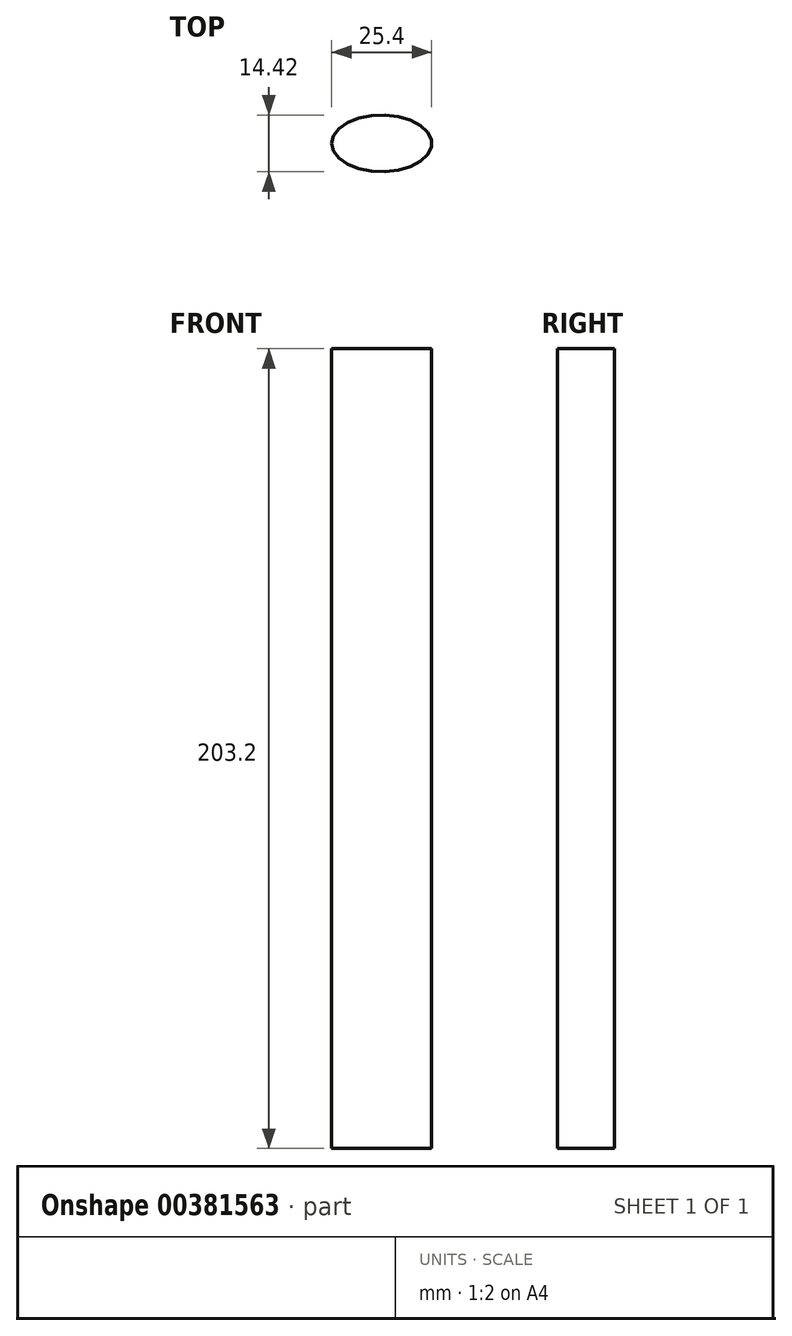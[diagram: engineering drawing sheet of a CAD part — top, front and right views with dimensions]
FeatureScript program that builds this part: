
annotation { "Feature Type Name" : "Feature", "Feature Type Description" : "" }
export const myFeature = defineFeature(function(context is Context, id is Id, definition is map)
    precondition{}
    {
        {
            var Q0;
            Q0=qCreatedBy(makeId("Top.planeOp"),FACE);
            var sketch = newSketch(context, id + "F0", { "sketchPlane" : qUnion([Q0])});
            skEllipse(sketch, "E0", {"center": v(0, 0) * mm, "majorRadius": 12.7 * mm, "minorRadius": 7.2 * mm, "majorAxis": v(-1, 0)});
            skFitSpline(sketch, "E1.0", {"points": [v(-11.32, 0.98) * mm, v(-11.49, 0) * mm, v(-11.32, -0.98) * mm, v(-10.87, -1.84) * mm, v(-10.3, -2.53) * mm, v(-9.57, -3.21) * mm, v(-8.41, -4.02) * mm, v(-6.95, -4.7) * mm, v(-5.63, -5.15) * mm, v(-4.22, -5.53) * mm, v(-2.73, -5.79) * mm, v(-1.18, -5.92) * mm, v(0, -5.95) * mm, v(1.18, -5.92) * mm, v(2.73, -5.79) * mm, v(4.22, -5.53) * mm, v(5.63, -5.15) * mm, v(6.95, -4.7) * mm, v(8.41, -4.02) * mm, v(9.57, -3.21) * mm, v(10.3, -2.53) * mm, v(10.87, -1.84) * mm, v(11.32, -0.98) * mm, v(11.49, 0) * mm, v(11.32, 0.98) * mm, v(10.87, 1.84) * mm, v(10.3, 2.53) * mm, v(9.57, 3.21) * mm, v(8.41, 4.02) * mm, v(6.95, 4.7) * mm, v(5.63, 5.15) * mm, v(4.22, 5.53) * mm, v(2.73, 5.79) * mm, v(1.18, 5.92) * mm, v(0, 5.95) * mm, v(-1.18, 5.92) * mm, v(-2.73, 5.79) * mm, v(-4.22, 5.53) * mm, v(-5.63, 5.15) * mm, v(-6.95, 4.7) * mm, v(-8.41, 4.02) * mm, v(-9.57, 3.21) * mm, v(-10.3, 2.53) * mm, v(-10.87, 1.84) * mm, v(-11.32, 0.98) * mm, v(-11.49, 0) * mm, v(-11.32, -0.98) * mm, v(-11.32, 0.98) * mm]});
            skSolve(sketch);
        }
        {
            var Q0;
            Q0=makeQuery(id+"F0.imprint","IMPRINT",FACE,{"disambiguationData":[TD([[makeQuery(id+"F0.imprint","IMPRINT",EDGE,{"derivedFrom":sQuery(id+"F0.wireOp",EDGE,"E0")}),1.0]])]});
            extrude(context, id + "F1", {"entities" : qUnion([Q0]), "depth" : 203.2 * mm});
        }
    });
